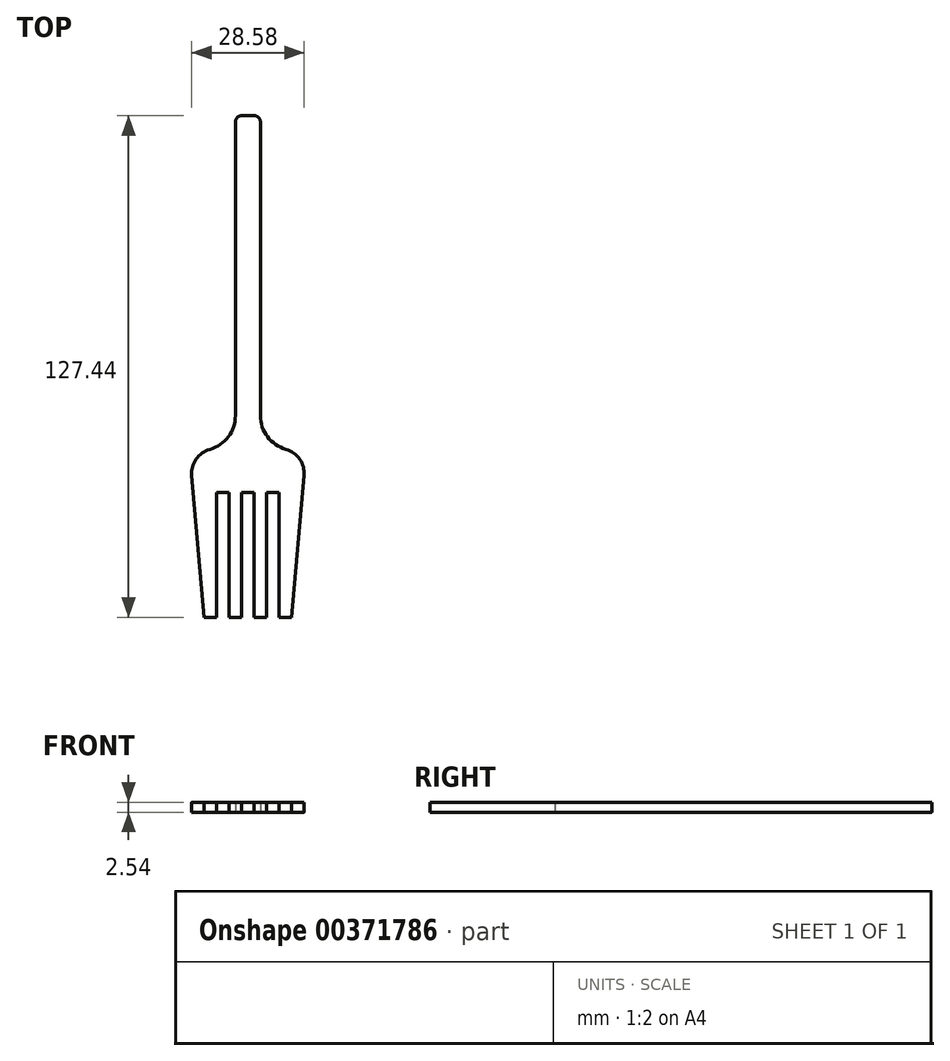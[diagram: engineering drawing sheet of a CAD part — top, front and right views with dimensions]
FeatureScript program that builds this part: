
annotation { "Feature Type Name" : "Feature", "Feature Type Description" : "" }
export const myFeature = defineFeature(function(context is Context, id is Id, definition is map)
    precondition{}
    {
        {
            var Q0;
            Q0=qCreatedBy(makeId("Top.planeOp"),FACE);
            var sketch = newSketch(context, id + "F0", { "sketchPlane" : qUnion([Q0])});
            skLineSegment(sketch, "E0", {"start": v(0, 71.82) * mm, "end": v(0, -51.24) * mm, "construction": true});
            skLineSegment(sketch, "E1", {"start": v(-3.17, 74.61) * mm, "end": v(-3.17, 0) * mm});
            skArc(sketch, "E2", {"start": v(-3.17, 0) * mm, "mid": v(-4.98, -5.37) * mm, "end": v(-9.66, -8.56) * mm});
            skArc(sketch, "E3", {"start": v(-9.66, -8.56) * mm, "mid": v(-13.16, -11.06) * mm, "end": v(-14.26, -15.22) * mm});
            skLineSegment(sketch, "E4", {"start": v(-14.26, -15.22) * mm, "end": v(-11.11, -51.24) * mm});
            skLineSegment(sketch, "E5", {"start": v(-11.11, -51.24) * mm, "end": v(-7.94, -51.24) * mm});
            skLineSegment(sketch, "E6", {"start": v(-7.94, -51.24) * mm, "end": v(-7.94, -19.49) * mm});
            skLineSegment(sketch, "E7", {"start": v(-7.94, -19.49) * mm, "end": v(-4.76, -19.49) * mm});
            skLineSegment(sketch, "E8", {"start": v(-4.76, -19.49) * mm, "end": v(-4.76, -51.24) * mm});
            skLineSegment(sketch, "E9", {"start": v(-4.76, -51.24) * mm, "end": v(-1.59, -51.24) * mm});
            skLineSegment(sketch, "E10", {"start": v(-1.59, -51.24) * mm, "end": v(-1.59, -19.49) * mm});
            skLineSegment(sketch, "E11", {"start": v(-1.59, -19.49) * mm, "end": v(0, -19.49) * mm});
            skLineSegment(sketch, "E12.MirrorCS", {"start": v(11.11, -51.24) * mm, "end": v(7.94, -51.24) * mm});
            skLineSegment(sketch, "E13.MirrorCS", {"start": v(7.94, -19.49) * mm, "end": v(4.76, -19.49) * mm});
            skLineSegment(sketch, "E14.MirrorCS", {"start": v(4.76, -51.24) * mm, "end": v(1.59, -51.24) * mm});
            skArc(sketch, "E15.MirrorCS", {"start": v(3.18, 0) * mm, "mid": v(4.98, -5.37) * mm, "end": v(9.66, -8.56) * mm});
            skArc(sketch, "E16.MirrorCS", {"start": v(9.66, -8.56) * mm, "mid": v(13.16, -11.06) * mm, "end": v(14.26, -15.22) * mm});
            skLineSegment(sketch, "E17.MirrorCS", {"start": v(3.18, 74.61) * mm, "end": v(3.17, 0) * mm});
            skLineSegment(sketch, "E18.MirrorCS", {"start": v(14.26, -15.22) * mm, "end": v(11.11, -51.24) * mm});
            skLineSegment(sketch, "E19.MirrorCS", {"start": v(7.94, -51.24) * mm, "end": v(7.94, -19.49) * mm});
            skLineSegment(sketch, "E20.MirrorCS", {"start": v(1.59, -51.24) * mm, "end": v(1.59, -19.49) * mm});
            skLineSegment(sketch, "E21.MirrorCS", {"start": v(4.76, -19.49) * mm, "end": v(4.76, -51.24) * mm});
            skLineSegment(sketch, "E22.MirrorCS", {"start": v(0, -110.8) * mm, "end": v(0, 12.26) * mm, "construction": true});
            skLineSegment(sketch, "E23.MirrorCS", {"start": v(1.59, -19.49) * mm, "end": v(0, -19.49) * mm});
            skArc(sketch, "E24", {"start": v(-3.17, 74.61) * mm, "mid": v(-2.71, 75.74) * mm, "end": v(-1.59, 76.2) * mm});
            skLineSegment(sketch, "E25", {"start": v(-1.59, 76.2) * mm, "end": v(1.59, 76.2) * mm});
            skArc(sketch, "E26", {"start": v(1.59, 76.2) * mm, "mid": v(2.71, 75.74) * mm, "end": v(3.17, 74.61) * mm});
            skSolve(sketch);
        }
        {
            var Q0;
            Q0=makeQuery(id+"F0.imprint","IMPRINT",FACE,{"disambiguationData":[TD([[makeQuery(id+"F0.imprint","IMPRINT",EDGE,{"derivedFrom":sQuery(id+"F0.wireOp",EDGE,"E1")}),1.0]])]});
            extrude(context, id + "F1", {"entities" : qUnion([Q0]), "depth" : 2.54 * mm});
        }
    });
